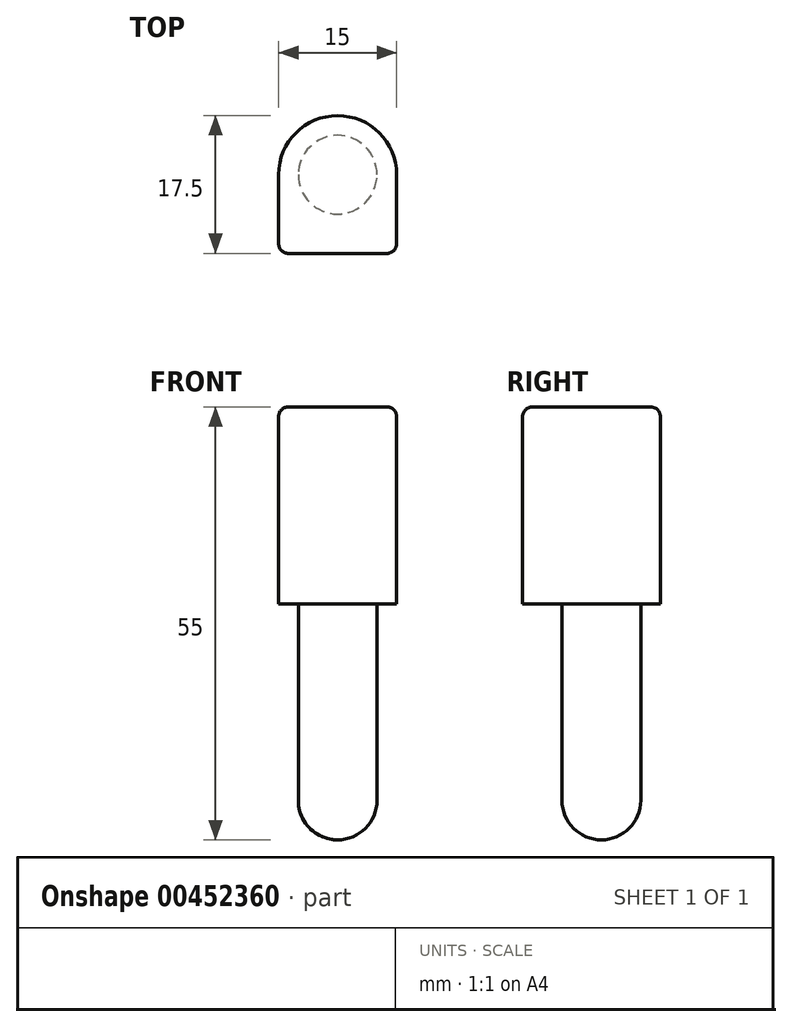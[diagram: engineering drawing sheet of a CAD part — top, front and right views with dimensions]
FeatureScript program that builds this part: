
annotation { "Feature Type Name" : "Feature", "Feature Type Description" : "" }
export const myFeature = defineFeature(function(context is Context, id is Id, definition is map)
    precondition{}
    {
        {
            var Q0;
            Q0=qCreatedBy(makeId("Top.planeOp"),FACE);
            var sketch = newSketch(context, id + "F0", { "sketchPlane" : qUnion([Q0])});
            skLineSegment(sketch, "E0", {"start": v(-7.5, -10) * mm, "end": v(7.5, -10) * mm});
            skLineSegment(sketch, "E1", {"start": v(-7.5, -10) * mm, "end": v(-7.5, 0) * mm});
            skLineSegment(sketch, "E2", {"start": v(7.5, -10) * mm, "end": v(7.5, 0) * mm});
            skArc(sketch, "E3", {"start": v(7.5, 0) * mm, "mid": v(0, 7.5) * mm, "end": v(-7.5, 0) * mm});
            skSolve(sketch);
        }
        {
            var Q0;
            Q0 = qSketchRegion(id + "F0", true);
            extrude(context, id + "F1", {"entities" : qUnion([Q0]), "depth" : 25 * mm});
        }
        {
            var Q0;
            Q0=makeQuery(id+"F1.opExtrude","SWEPT_EDGE",EDGE,{"disambiguationData":[OSD([sQuery(id+"F0.wireOp",EDGE,"E0"),sQuery(id+"F0.wireOp",EDGE,"E2")])]});
            var Q1;
            Q1=makeQuery(id+"F1.opExtrude","CAP_EDGE",EDGE,{"disambiguationData":[OSD([sQuery(id+"F0.wireOp",EDGE,"E0")])],"isStart":false});
            var Q2;
            Q2=makeQuery(id+"F1.opExtrude","CAP_EDGE",EDGE,{"disambiguationData":[OSD([sQuery(id+"F0.wireOp",EDGE,"E2")])],"isStart":false});
            var Q3;
            Q3=makeQuery(id+"F1.opExtrude","SWEPT_EDGE",EDGE,{"disambiguationData":[OSD([sQuery(id+"F0.wireOp",EDGE,"E0"),sQuery(id+"F0.wireOp",EDGE,"E1")])]});
            fillet(context, id + "F2", {"entities" : qUnion([Q0, Q1, Q2, Q3]), "radius" : 1.25 * mm, "tangentPropagation" : true, "allowEdgeOverflow" : false});
        }
        {
            var Q0;
            Q0=makeQuery(id+"F1.opExtrude","CAP_FACE",FACE,{"disambiguationData":[OSD([sQuery(id+"F0.wireOp",EDGE,"E0"),sQuery(id+"F0.wireOp",EDGE,"E1"),sQuery(id+"F0.wireOp",EDGE,"E2"),sQuery(id+"F0.wireOp",EDGE,"E3")])],"isStart":true});
            var sketch = newSketch(context, id + "F3", { "sketchPlane" : qUnion([Q0])});
            skCircle(sketch, "E4", {"center": v(0, 0) * mm, "radius": 5 * mm});
            skSolve(sketch);
        }
        {
            var Q0;
            Q0 = qSketchRegion(id + "F3", true);
            extrude(context, id + "F4", {"entities" : qUnion([Q0]), "operationType" : NewBodyOperationType.ADD, "depth" : 30 * mm});
        }
        {
            var Q0;
            Q0=makeQuery(id+"F4.opExtrude","CAP_EDGE",EDGE,{"disambiguationData":[OSD([sQuery(id+"F3.wireOp",EDGE,"E4")])],"isStart":false});
            fillet(context, id + "F5", {"entities" : qUnion([Q0]), "radius" : 5 * mm, "tangentPropagation" : true, "allowEdgeOverflow" : false});
        }
    });
